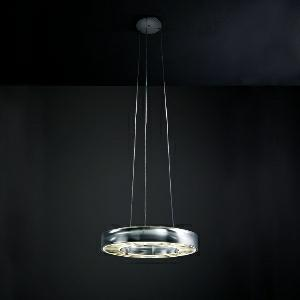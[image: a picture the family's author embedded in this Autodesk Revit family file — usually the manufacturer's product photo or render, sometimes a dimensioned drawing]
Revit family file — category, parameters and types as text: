
# Revit family: spectral_iris_iris-p-led_4080-840-t
name_source: partatom
category: Lighting Fixtures
revit_build: Autodesk Revit 2016 (Build: 20150220_1215(x64)
units: mm (PartAtom-declared; Revit-internal decimal feet)

## family parameters
Cut with Voids When Loaded = No
Host = Face
Light Source = No
Part Type = Normal
Room Calculation Point = No
Round Connector Dimension = Use Diameter
Shared = No

## types (1)
- SPECTRAL IRIS (1 x )
    Apparent Load = 0 VA
    Approval mark = CE
    CIE Flux Codes = 57 76 90 43 100
    Control Gear = Electronic transformer
    Default Elevation = 1800 mm
    Description = SPI0000030AY
Pendant luminaire IRIS

Design:
Direct-indirect beam ring-shaped luminaire made of highly transparent plastic. The rotationally symmetrical, flame retardant and impact resistant luminaire
housing is suspended from the ceiling. Transparent insect protection ring separately available as an accessory. Glare reduction by means of round diffuser panel made of highly transparent plastic with microprism structure which clips in from below. Patented suspension of the housing on three transparent double insulated single cables which simultaneously serve as connecting wires. Standard suspension length 3000 mm, individual shortening possible. Fixture of the connecting cables at the round ceiling housing with heat-resistant wiring. All metal parts are powder coated. 

Colour: housing – transparent; ceiling box similar to RAL 9016 white silk matt. Colour accentuation of the housing possible by inserting a separately available colour inlay film. 

LED: 3 LED ring segment boards for direct lighting component and 3 LED ring segment boards for direct lighting component. Light colours 830, 840.

Protection rating IP20, safety class I.
    Height = 50 mm
    Lamp = 1 x
    Lamp count = 1
    Length = 360 mm
    Luminous efficacy = 0 lm/W
    Manufacturer = Ridi
    ModVariant = No
    Model = IRIS-P-LED 4080-840-T
    Mounting Place = Ceiling
    Mounting Type = Pendant
    Number of Poles = 1
    OnlyDefault = Yes
    Power Factor = 1
    Product Name = SPECTRAL IRIS
    Product group = Pendant luminaire
    ProductGroupID = 9
    Protection Class = Protection class
    Protection Degree = IP 20
    RlxData = <blob elided: 41453 chars, md5=22baad3a>
    Socket = socket
    Standby Power = 0 W
    System Light Flux = 0 lm
    System Power = 0 W
    Type Image = 001_pro_iri_pen_01_01700156_001.jpg
    URL = http://reluxnet.relux.com
    VarID = 1
    Voltage = 0 V
    Weight = 0.00 kg
    Width = 0 mm  [stored 0 ft]

note: [stored X ft] marks values corroborated as IEEE doubles in the binary element streams (Revit-internal decimal feet)

## geometry (parser evidence)
native form markers: Sweep x11
no freeform markers — native parametric forms only
